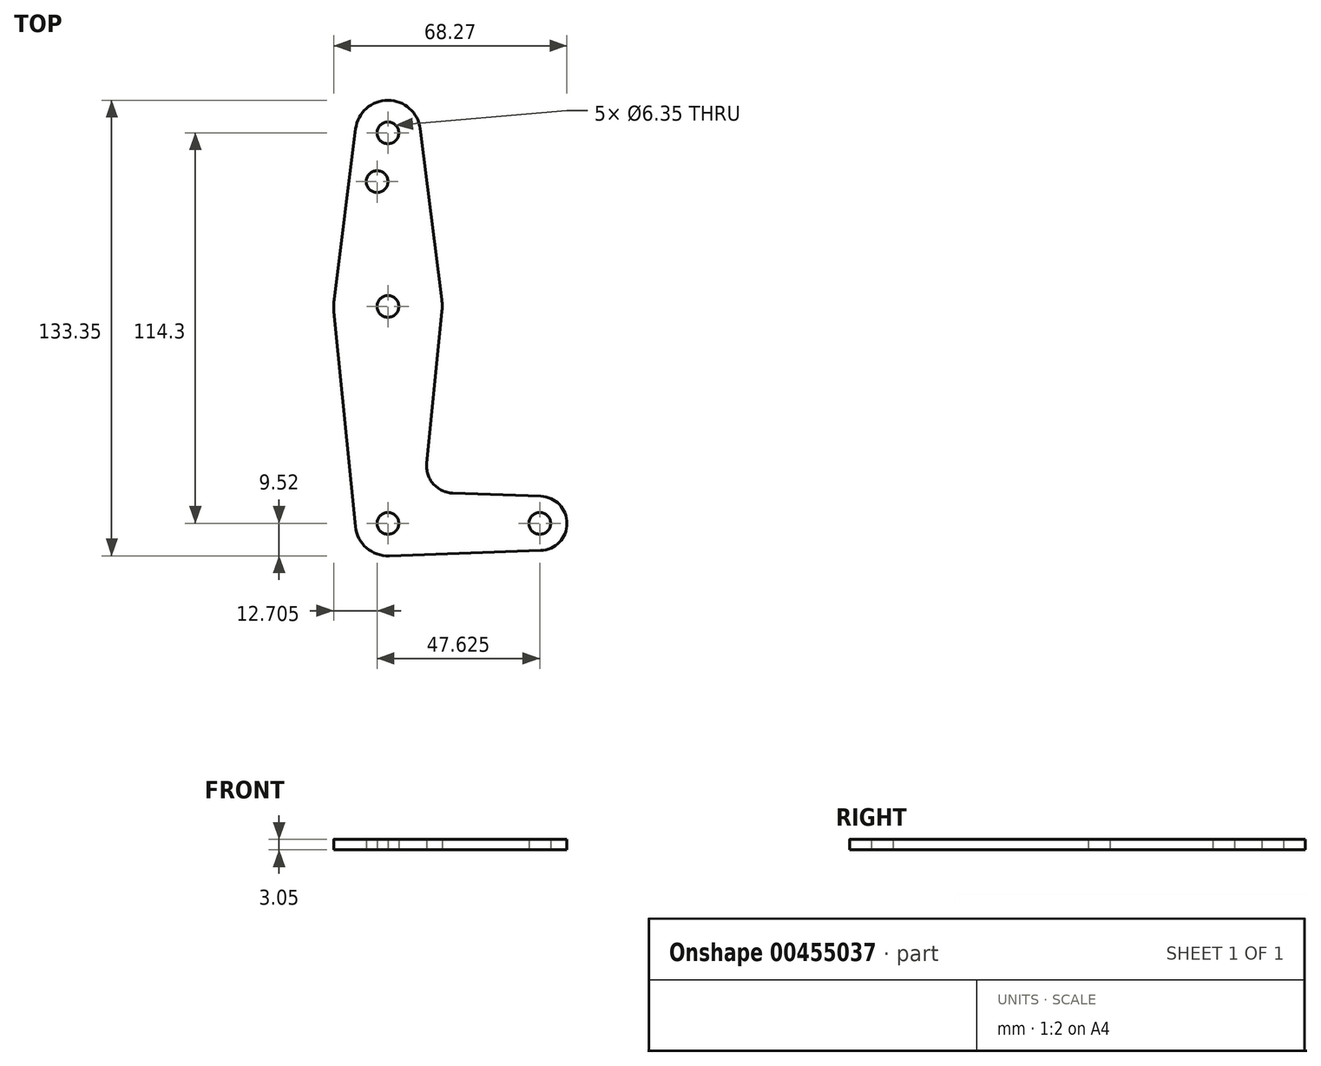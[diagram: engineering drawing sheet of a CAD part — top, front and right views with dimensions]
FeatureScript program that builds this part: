
annotation { "Feature Type Name" : "Feature", "Feature Type Description" : "" }
export const myFeature = defineFeature(function(context is Context, id is Id, definition is map)
    precondition{}
    {
        {
            var Q0;
            Q0=qCreatedBy(makeId("Top.planeOp"),FACE);
            var sketch = newSketch(context, id + "F0", { "sketchPlane" : qUnion([Q0])});
            skLineSegment(sketch, "E0", {"start": v(0, 0) * mm, "end": v(0, 114.3) * mm, "construction": true});
            skLineSegment(sketch, "E1", {"start": v(0, 0) * mm, "end": v(44.45, 0) * mm, "construction": true});
            skCircle(sketch, "E2", {"center": v(0, 0) * mm, "radius": 9.53 * mm});
            skCircle(sketch, "E3", {"center": v(0, 114.3) * mm, "radius": 9.53 * mm});
            skCircle(sketch, "E4", {"center": v(0, 63.5) * mm, "radius": 15.88 * mm});
            skCircle(sketch, "E5", {"center": v(44.45, 0) * mm, "radius": 7.94 * mm});
            skLineSegment(sketch, "E6", {"start": v(0, 63.5) * mm, "end": v(0, 0) * mm, "construction": true});
            skLineSegment(sketch, "E7", {"start": v(-9.45, 115.5) * mm, "end": v(-15.75, 65.48) * mm});
            skLineSegment(sketch, "E8", {"start": v(-15.8, 61.91) * mm, "end": v(-9.48, -0.95) * mm});
            skLineSegment(sketch, "E9", {"start": v(9.45, 115.5) * mm, "end": v(15.75, 65.48) * mm});
            skLineSegment(sketch, "E10", {"start": v(15.8, 61.91) * mm, "end": v(11.34, 17.6) * mm});
            skLineSegment(sketch, "E11", {"start": v(18.97, 8.85) * mm, "end": v(44.73, 7.93) * mm});
            skLineSegment(sketch, "E12", {"start": v(0.34, -9.52) * mm, "end": v(44.73, -7.93) * mm});
            skCircle(sketch, "E13", {"center": v(0, 114.3) * mm, "radius": 3.18 * mm});
            skCircle(sketch, "E14", {"center": v(0, 63.5) * mm, "radius": 3.18 * mm});
            skCircle(sketch, "E15", {"center": v(0, 0) * mm, "radius": 3.18 * mm});
            skCircle(sketch, "E16", {"center": v(44.45, 0) * mm, "radius": 3.18 * mm});
            skArc(sketch, "E17.filletArc", {"start": v(11.34, 17.6) * mm, "mid": v(13.26, 11.57) * mm, "end": v(18.97, 8.85) * mm});
            skLineSegment(sketch, "E18", {"start": v(0, 63.5) * mm, "end": v(-3.18, 63.5) * mm, "construction": true});
            skLineSegment(sketch, "E19", {"start": v(0, 100.03) * mm, "end": v(-3.18, 100.03) * mm, "construction": true});
            skCircle(sketch, "E20", {"center": v(-3.18, 100.03) * mm, "radius": 3.18 * mm});
            skLineSegment(sketch, "E21", {"start": v(-3.17, 100.03) * mm, "end": v(-3.18, 63.5) * mm, "construction": true});
            skSolve(sketch);
        }
        {
            var Q0;
            Q0 = qSketchRegion(id + "F0", true);
            extrude(context, id + "F1", {"entities" : qUnion([Q0]), "depth" : 3.05 * mm});
        }
    });
